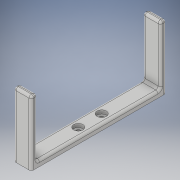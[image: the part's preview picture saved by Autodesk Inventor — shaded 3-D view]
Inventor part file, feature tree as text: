
AUTODESK INVENTOR PART (.ipt)
format: ipt  version: 2019.4 (Build 234330000, 330)  size: 189,440 bytes
history: native  units: mm
features: extrude x4, sketch x4, fillet x3
ambient origin geometry x8: Origin, YZ Plane, XZ Plane, XY Plane, X Axis, Y Axis, Z Axis, Center Point
bodies: Solid1 (feature_tree)
feature tree (11):
  extrude  "Extrusion1"  Depth=15.0mm
  extrude  "Extrusion2"  Depth=10.0mm
  extrude  "Extrusion3"  Depth=10.0mm
  extrude  "Extrusion4"  Depth=5.0mm TaperAngle=0.0deg
  fillet  "Fillet1"  Radius=8.0mm
  fillet  "Fillet2"  Radius=8.0mm
  fillet  "Fillet3"  Radius=3.0mm
  sketch  "Sketch1"  dims[d0=115.0mm d1=15.0mm]
  sketch  "Sketch2"  dims[d2=5.0mm d3=0.0mm d4=10.0mm]
  sketch  "Sketch3"  dims[d5=10.0mm d6=3.5mm]
  sketch  "Sketch4"  dims[d7=3.5mm d8=5.0mm d9=0.0mm d10=8.0mm d11=8.0mm d12=3.0mm d13=0.0mm d14=15.0mm d15=5.0mm d16=15.0mm d17=5.0mm d18=50.0mm d19=0.0mm d20=2.0mm d21=2.0mm d22=2.0mm]
